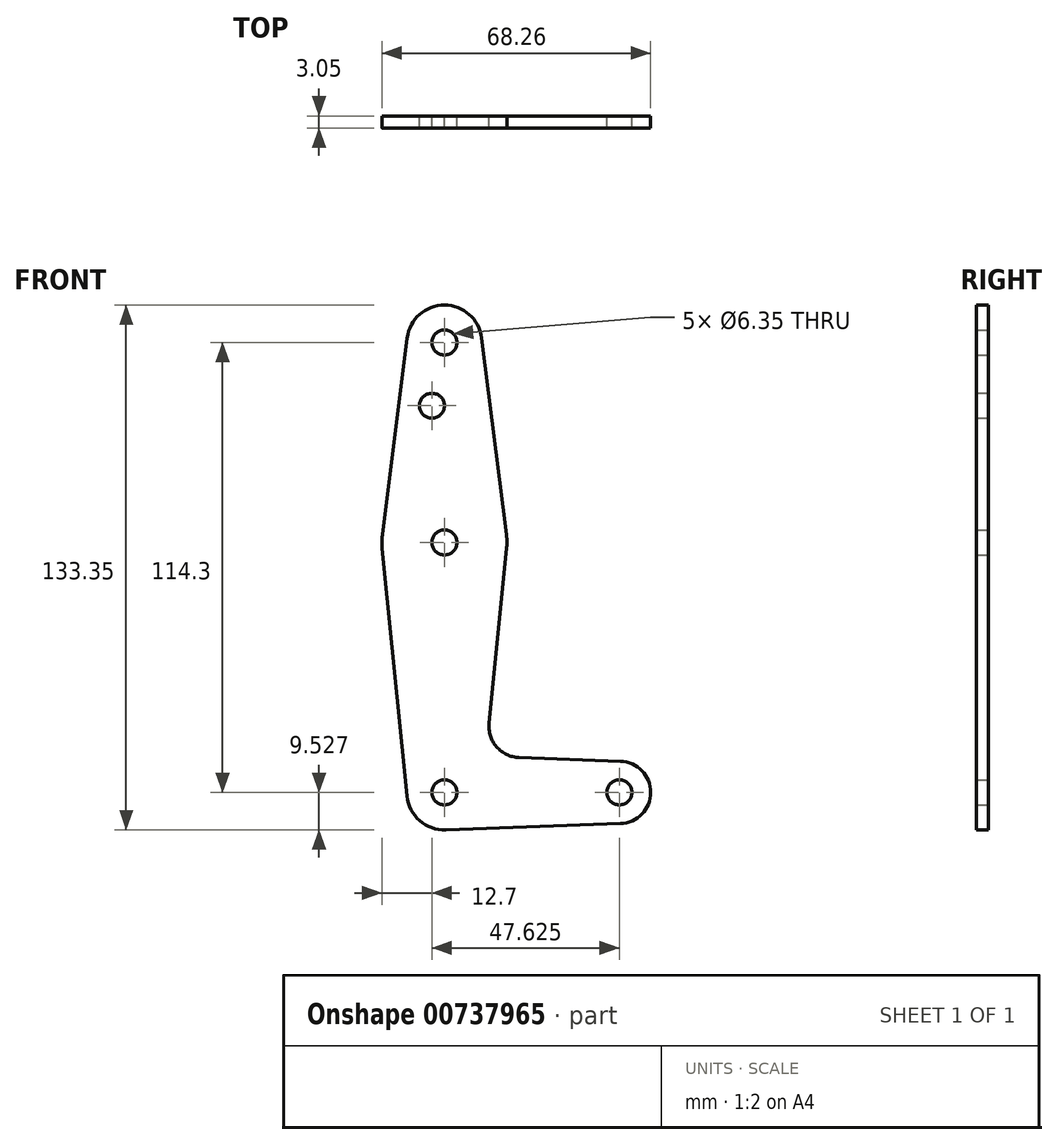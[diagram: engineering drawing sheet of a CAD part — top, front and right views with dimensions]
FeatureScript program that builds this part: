
annotation { "Feature Type Name" : "Feature", "Feature Type Description" : "" }
export const myFeature = defineFeature(function(context is Context, id is Id, definition is map)
    precondition{}
    {
        {
            var Q0;
            Q0=qCreatedBy(makeId("Front.planeOp"),FACE);
            var sketch = newSketch(context, id + "F0", { "sketchPlane" : qUnion([Q0])});
            skLineSegment(sketch, "E0", {"start": v(-43.16, 49.53) * mm, "end": v(-43.16, -64.77) * mm, "construction": true});
            skLineSegment(sketch, "E1", {"start": v(-43.16, -64.77) * mm, "end": v(1.29, -64.77) * mm});
            skCircle(sketch, "E2", {"center": v(-43.16, 49.53) * mm, "radius": 9.53 * mm});
            skCircle(sketch, "E3", {"center": v(1.29, -64.77) * mm, "radius": 7.94 * mm});
            skCircle(sketch, "E4", {"center": v(-43.16, -1.27) * mm, "radius": 15.88 * mm});
            skLineSegment(sketch, "E5", {"start": v(-52.62, 50.72) * mm, "end": v(-58.92, 0.71) * mm});
            skLineSegment(sketch, "E6", {"start": v(-33.71, 50.72) * mm, "end": v(-27.41, 0.71) * mm});
            skCircle(sketch, "E7", {"center": v(-43.16, -64.77) * mm, "radius": 9.53 * mm});
            skLineSegment(sketch, "E8", {"start": v(-58.96, -2.86) * mm, "end": v(-52.64, -65.73) * mm});
            skPoint(sketch, "E9.startSnap0", {"position": v(-43.16, -7.62) * mm});
            skLineSegment(sketch, "E10", {"start": v(-27.37, -2.86) * mm, "end": v(-31.82, -47.18) * mm});
            skLineSegment(sketch, "E11", {"start": v(-24.2, -55.92) * mm, "end": v(1.57, -56.84) * mm});
            skLineSegment(sketch, "E12", {"start": v(1.57, -72.7) * mm, "end": v(-42.82, -74.3) * mm});
            skCircle(sketch, "E13", {"center": v(-43.16, 49.53) * mm, "radius": 3.18 * mm});
            skCircle(sketch, "E14", {"center": v(-43.16, -1.27) * mm, "radius": 3.18 * mm});
            skCircle(sketch, "E15", {"center": v(-43.16, -64.77) * mm, "radius": 3.18 * mm});
            skCircle(sketch, "E16", {"center": v(1.29, -64.77) * mm, "radius": 3.18 * mm});
            skCircle(sketch, "E17", {"center": v(-46.34, 33.47) * mm, "radius": 3.18 * mm});
            skArc(sketch, "E18.filletArc", {"start": v(-31.82, -47.18) * mm, "mid": v(-29.9, -53.2) * mm, "end": v(-24.2, -55.92) * mm});
            skSolve(sketch);
        }
        {
            var Q0;
            {var subQ0=sQuery(id+"F0.wireOp",EDGE,"E2");var subQ1=makeQuery(id+"F0.imprint","INTERSECT",VERTEX,{"derivedFrom":[subQ0,sQuery(id+"F0.wireOp",EDGE,"E5")]});Q0=makeQuery(id+"F0.imprint","IMPRINT",FACE,{"disambiguationData":[TD([[makeQuery(id+"F0.imprint","IMPRINT",EDGE,{"disambiguationData":[TD([[subQ1,1.0]])],"derivedFrom":subQ0}),1.0]])]});}
            var Q1;
            {var subQ0=sQuery(id+"F0.wireOp",EDGE,"E3");var subQ1=makeQuery(id+"F0.imprint","INTERSECT",VERTEX,{"derivedFrom":[subQ0,sQuery(id+"F0.wireOp",EDGE,"E11")]});Q1=makeQuery(id+"F0.imprint","IMPRINT",FACE,{"disambiguationData":[TD([[makeQuery(id+"F0.imprint","IMPRINT",EDGE,{"disambiguationData":[TD([[subQ1,-1.0]])],"derivedFrom":subQ0}),1.0]])]});}
            var Q2;
            {var subQ0=sQuery(id+"F0.wireOp",EDGE,"E4");var subQ1=makeQuery(id+"F0.imprint","INTERSECT",VERTEX,{"derivedFrom":[subQ0,sQuery(id+"F0.wireOp",EDGE,"E5")]});Q2=makeQuery(id+"F0.imprint","IMPRINT",FACE,{"disambiguationData":[TD([[makeQuery(id+"F0.imprint","IMPRINT",EDGE,{"disambiguationData":[TD([[subQ1,1.0]])],"derivedFrom":subQ0}),1.0]])]});}
            var Q3;
            {var subQ0=sQuery(id+"F0.wireOp",EDGE,"E10");var subQ1=sQuery(id+"F0.wireOp",EDGE,"E1");var subQ2=makeQuery(id+"F0.imprint","INTERSECT",VERTEX,{"derivedFrom":[subQ1,subQ0]});Q3=makeQuery(id+"F0.imprint","IMPRINT",FACE,{"disambiguationData":[TD([[makeQuery(id+"F0.imprint","IMPRINT",EDGE,{"disambiguationData":[TD([[subQ2,-1.0]])],"derivedFrom":subQ1}),1.0]])]});}
            var Q4;
            {var subQ5=sQuery(id+"F0.wireOp",EDGE,"E8");Q4=makeQuery(id+"F0.imprint","IMPRINT",FACE,{"disambiguationData":[TD([[makeQuery(id+"F0.imprint","IMPRINT",EDGE,{"derivedFrom":subQ5}),1.0]])]});}
            var Q5;
            {var subQ0=sQuery(id+"F0.wireOp",EDGE,"E7");var subQ1=makeQuery(id+"F0.imprint","INTERSECT",VERTEX,{"derivedFrom":[subQ0,sQuery(id+"F0.wireOp",EDGE,"E11")]});Q5=makeQuery(id+"F0.imprint","IMPRINT",FACE,{"disambiguationData":[TD([[makeQuery(id+"F0.imprint","IMPRINT",EDGE,{"disambiguationData":[TD([[subQ1,1.0]])],"derivedFrom":subQ0}),1.0]])]});}
            var Q6;
            {var subQ0=sQuery(id+"F0.wireOp",EDGE,"E12");Q6=makeQuery(id+"F0.imprint","IMPRINT",FACE,{"disambiguationData":[TD([[makeQuery(id+"F0.imprint","IMPRINT",EDGE,{"derivedFrom":subQ0}),-1.0]])]});}
            var Q7;
            {var subQ0=sQuery(id+"F0.wireOp",EDGE,"E10");var subQ1=sQuery(id+"F0.wireOp",EDGE,"E1");var subQ2=makeQuery(id+"F0.imprint","INTERSECT",VERTEX,{"derivedFrom":[subQ1,subQ0]});Q7=makeQuery(id+"F0.imprint","IMPRINT",FACE,{"disambiguationData":[TD([[makeQuery(id+"F0.imprint","IMPRINT",EDGE,{"disambiguationData":[TD([[subQ2,1.0]])],"derivedFrom":subQ1}),1.0]])]});}
            var Q8;
            {var subQ0=sQuery(id+"F0.wireOp",EDGE,"E5");Q8=makeQuery(id+"F0.imprint","IMPRINT",FACE,{"disambiguationData":[TD([[makeQuery(id+"F0.imprint","IMPRINT",EDGE,{"derivedFrom":subQ0}),1.0]])]});}
            extrude(context, id + "F1", {"entities" : qUnion([Q0, Q1, Q2, Q3, Q4, Q5, Q6, Q7, Q8]), "depth" : 3.05 * mm, "offsetDistance" : 25.4 * mm});
        }
    });
